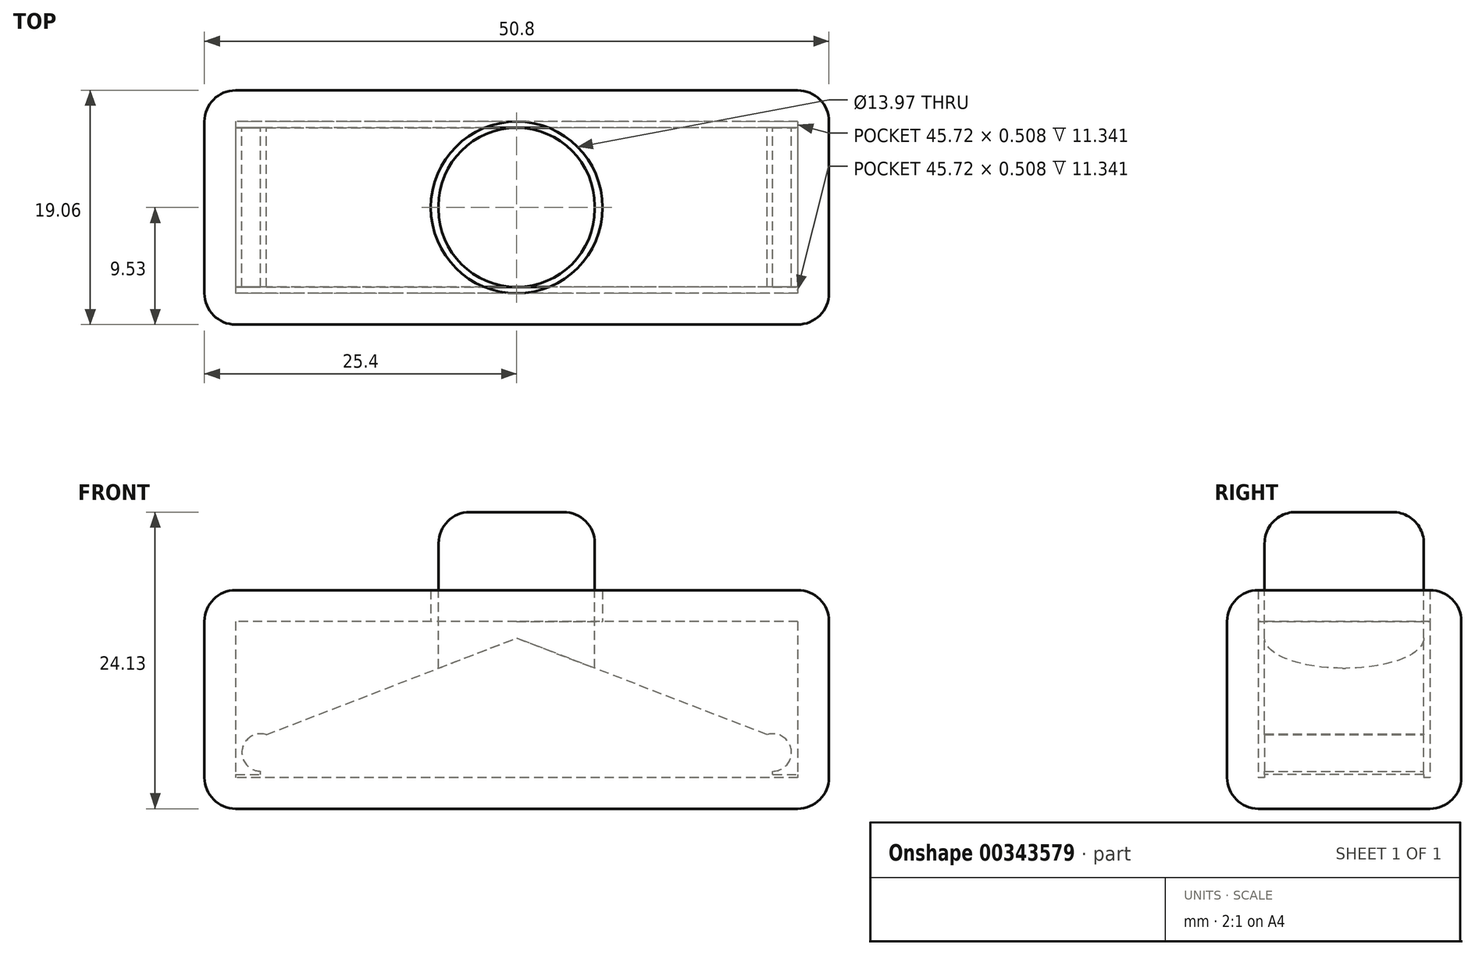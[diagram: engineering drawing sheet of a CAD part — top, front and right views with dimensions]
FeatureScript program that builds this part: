
annotation { "Feature Type Name" : "Feature", "Feature Type Description" : "" }
export const myFeature = defineFeature(function(context is Context, id is Id, definition is map)
    precondition{}
    {
        {
            var Q0;
            Q0=qCreatedBy(makeId("Top.planeOp"),FACE);
            var sketch = newSketch(context, id + "F0", { "sketchPlane" : qUnion([Q0])});
            skLineSegment(sketch, "E0.bottom", {"start": v(25.4, 9.53) * mm, "end": v(-25.4, 9.53) * mm});
            skLineSegment(sketch, "E0.top", {"start": v(25.4, -9.53) * mm, "end": v(-25.4, -9.53) * mm});
            skLineSegment(sketch, "E0.left", {"start": v(25.4, 9.53) * mm, "end": v(25.4, -9.53) * mm});
            skLineSegment(sketch, "E0.right", {"start": v(-25.4, 9.53) * mm, "end": v(-25.4, -9.53) * mm});
            skPoint(sketch, "E0.middle", {"position": v(0, 0) * mm});
            skLineSegment(sketch, "E1.bottom", {"start": v(22.86, 6.99) * mm, "end": v(-22.86, 6.99) * mm});
            skLineSegment(sketch, "E1.top", {"start": v(22.86, -6.99) * mm, "end": v(-22.86, -6.99) * mm});
            skLineSegment(sketch, "E1.left", {"start": v(22.86, 6.98) * mm, "end": v(22.86, -6.99) * mm});
            skLineSegment(sketch, "E1.right", {"start": v(-22.86, 6.99) * mm, "end": v(-22.86, -6.98) * mm});
            skSolve(sketch);
        }
        {
            var Q0;
            Q0 = qSketchRegion(id + "F0", true);
            extrude(context, id + "F1", {"entities" : qUnion([Q0]), "depth" : 12.7 * mm, "offsetDistance" : 25.4 * mm});
        }
        {
            var Q0;
            Q0=makeQuery(id+"F1.opExtrude","CAP_FACE",FACE,{"disambiguationData":[OSD([sQuery(id+"F0.wireOp",EDGE,"E0.bottom"),sQuery(id+"F0.wireOp",EDGE,"E0.top"),sQuery(id+"F0.wireOp",EDGE,"E0.left"),sQuery(id+"F0.wireOp",EDGE,"E0.right"),sQuery(id+"F0.wireOp",EDGE,"E1.bottom"),sQuery(id+"F0.wireOp",EDGE,"E1.top"),sQuery(id+"F0.wireOp",EDGE,"E1.left"),sQuery(id+"F0.wireOp",EDGE,"E1.right")])],"isStart":true});
            var sketch = newSketch(context, id + "F2", { "sketchPlane" : qUnion([Q0])});
            skLineSegment(sketch, "E2.bottom", {"start": v(25.4, 9.53) * mm, "end": v(-25.4, 9.53) * mm});
            skLineSegment(sketch, "E2.top", {"start": v(25.4, -9.53) * mm, "end": v(-25.4, -9.53) * mm});
            skLineSegment(sketch, "E2.left", {"start": v(25.4, 9.53) * mm, "end": v(25.4, -9.53) * mm});
            skLineSegment(sketch, "E2.right", {"start": v(-25.4, 9.53) * mm, "end": v(-25.4, -9.53) * mm});
            skSolve(sketch);
        }
        {
            var Q0;
            Q0 = qSketchRegion(id + "F2", true);
            extrude(context, id + "F3", {"entities" : qUnion([Q0]), "operationType" : NewBodyOperationType.ADD, "depth" : 2.54 * mm, "offsetDistance" : 25.4 * mm});
        }
        {
            var Q0;
            Q0=makeQuery(id+"F1.opExtrude","SWEPT_FACE",FACE,{"disambiguationData":[OSD([sQuery(id+"F0.wireOp",EDGE,"E1.bottom")])]});
            var sketch = newSketch(context, id + "F4", { "sketchPlane" : qUnion([Q0])});
            skLineSegment(sketch, "E3.bottom", {"start": v(-25.4, -2.54) * mm, "end": v(25.4, -2.54) * mm});
            skLineSegment(sketch, "E3.top", {"start": v(-25.4, -2.54) * mm, "end": v(25.4, -2.54) * mm});
            skLineSegment(sketch, "E3.left", {"start": v(-25.4, -2.54) * mm, "end": v(-25.4, -2.54) * mm});
            skLineSegment(sketch, "E3.right", {"start": v(25.4, -2.54) * mm, "end": v(25.4, -2.54) * mm});
            skLineSegment(sketch, "E4.top", {"start": v(-25.4, 0.25) * mm, "end": v(25.4, 0.25) * mm});
            skLineSegment(sketch, "E4.left", {"start": v(-25.4, -2.54) * mm, "end": v(-25.4, 0.25) * mm});
            skLineSegment(sketch, "E4.right", {"start": v(25.4, -2.54) * mm, "end": v(25.4, 0.25) * mm});
            skLineSegment(sketch, "E5", {"start": v(25.4, 12.7) * mm, "end": v(-25.4, 12.7) * mm});
            skLineSegment(sketch, "E6.bottom", {"start": v(6.35, 7.62) * mm, "end": v(-6.35, 7.62) * mm});
            skLineSegment(sketch, "E6.top", {"start": v(6.35, 17.78) * mm, "end": v(-6.35, 17.78) * mm});
            skLineSegment(sketch, "E6.left", {"start": v(6.35, 7.62) * mm, "end": v(6.35, 17.78) * mm});
            skLineSegment(sketch, "E6.right", {"start": v(-6.35, 7.62) * mm, "end": v(-6.35, 17.78) * mm});
            skPoint(sketch, "E6.middle", {"position": v(0, 12.7) * mm});
            skLineSegment(sketch, "E7", {"start": v(6.35, 7.62) * mm, "end": v(5.08, 7.62) * mm});
            skLineSegment(sketch, "E8", {"start": v(6.35, 7.62) * mm, "end": v(6.35, 8.89) * mm});
            skLineSegment(sketch, "E9", {"start": v(-6.35, 7.62) * mm, "end": v(-5.08, 7.62) * mm});
            skLineSegment(sketch, "E10", {"start": v(-6.35, 7.62) * mm, "end": v(-6.35, 8.89) * mm});
            skLineSegment(sketch, "E11", {"start": v(-25.4, 0.25) * mm, "end": v(-20.83, 0.25) * mm});
            skLineSegment(sketch, "E12", {"start": v(-20.83, 0.25) * mm, "end": v(-20.83, 2.03) * mm});
            skCircle(sketch, "E13", {"center": v(-20.83, 2.03) * mm, "radius": 1.52 * mm});
            skLineSegment(sketch, "E14", {"start": v(-20.83, 2.03) * mm, "end": v(-19.56, 2.03) * mm});
            skLineSegment(sketch, "E15", {"start": v(-20.83, 2.03) * mm, "end": v(-20.83, 3.3) * mm});
            skLineSegment(sketch, "E16", {"start": v(-20.83, 3.3) * mm, "end": v(-6.35, 8.89) * mm});
            skLineSegment(sketch, "E17", {"start": v(25.4, -2.54) * mm, "end": v(20.83, -2.54) * mm});
            skLineSegment(sketch, "E18", {"start": v(20.83, -2.54) * mm, "end": v(20.83, 2.03) * mm});
            skCircle(sketch, "E19", {"center": v(20.83, 2.03) * mm, "radius": 1.52 * mm});
            skLineSegment(sketch, "E20", {"start": v(20.83, 2.03) * mm, "end": v(20.83, 3.3) * mm});
            skLineSegment(sketch, "E21", {"start": v(20.83, 2.03) * mm, "end": v(19.56, 2.03) * mm});
            skLineSegment(sketch, "E22", {"start": v(20.83, 3.3) * mm, "end": v(6.35, 8.89) * mm});
            skLineSegment(sketch, "E23", {"start": v(19.56, 2.03) * mm, "end": v(5.08, 7.62) * mm});
            skLineSegment(sketch, "E24", {"start": v(-19.56, 2.03) * mm, "end": v(-5.08, 7.62) * mm});
            skLineSegment(sketch, "E25.bottom", {"start": v(-6.35, 17.78) * mm, "end": v(6.35, 17.78) * mm});
            skLineSegment(sketch, "E25.top", {"start": v(-6.35, 21.59) * mm, "end": v(6.35, 21.59) * mm});
            skLineSegment(sketch, "E25.left", {"start": v(-6.35, 17.78) * mm, "end": v(-6.35, 21.59) * mm});
            skLineSegment(sketch, "E25.right", {"start": v(6.35, 17.78) * mm, "end": v(6.35, 21.59) * mm});
            skSolve(sketch);
        }
        {
            var Q0;
            Q0 = qSketchRegion(id + "F4", true);
            extrude(context, id + "F5", {"entities" : qUnion([Q0]), "operationType" : NewBodyOperationType.ADD, "depth" : 13.46 * mm, "offsetDistance" : 25.4 * mm, "hasSecondDirection" : true, "secondDirectionOppositeDirection" : true, "secondDirectionDepth" : -0.5 * mm});
        }
        {
            var Q0;
            Q0=makeQuery(id+"F5.opExtrude","CAP_EDGE",EDGE,{"disambiguationData":[OSD([sQuery(id+"F4.wireOp",EDGE,"E6.right")])],"isStart":false});
            var Q1;
            Q1=makeQuery(id+"F5.opExtrude","CAP_EDGE",EDGE,{"disambiguationData":[OSD([sQuery(id+"F4.wireOp",EDGE,"E6.left")])],"isStart":false});
            var Q2;
            Q2=makeQuery(id+"F5.opExtrude","CAP_EDGE",EDGE,{"disambiguationData":[OSD([sQuery(id+"F4.wireOp",EDGE,"E6.left")])],"isStart":true});
            var Q3;
            Q3=makeQuery(id+"F5.opExtrude","CAP_EDGE",EDGE,{"disambiguationData":[OSD([sQuery(id+"F4.wireOp",EDGE,"E6.right")])],"isStart":true});
            fillet(context, id + "F6", {"entities" : qUnion([Q0, Q1, Q2, Q3]), "tangentPropagation" : true, "radius" : 6.35 * mm, "defaultsChanged" : true, "vertexSettings" : [], "allowEdgeOverflow" : false});
        }
        {
            var Q0;
            Q0=makeQuery(id+"F1.opExtrude","CAP_FACE",FACE,{"disambiguationData":[OSD([sQuery(id+"F0.wireOp",EDGE,"E0.bottom"),sQuery(id+"F0.wireOp",EDGE,"E0.top"),sQuery(id+"F0.wireOp",EDGE,"E0.left"),sQuery(id+"F0.wireOp",EDGE,"E0.right"),sQuery(id+"F0.wireOp",EDGE,"E1.bottom"),sQuery(id+"F0.wireOp",EDGE,"E1.top"),sQuery(id+"F0.wireOp",EDGE,"E1.left"),sQuery(id+"F0.wireOp",EDGE,"E1.right")])],"isStart":false});
            var sketch = newSketch(context, id + "F7", { "sketchPlane" : qUnion([Q0])});
            skLineSegment(sketch, "E26.bottom", {"start": v(-25.4, 9.53) * mm, "end": v(25.4, 9.53) * mm});
            skLineSegment(sketch, "E26.top", {"start": v(-25.4, -9.53) * mm, "end": v(25.4, -9.53) * mm});
            skLineSegment(sketch, "E26.left", {"start": v(-25.4, 9.53) * mm, "end": v(-25.4, -9.53) * mm});
            skLineSegment(sketch, "E26.right", {"start": v(25.4, 9.53) * mm, "end": v(25.4, -9.53) * mm});
            skCircle(sketch, "E27", {"center": v(0, 0) * mm, "radius": 6.99 * mm});
            skSolve(sketch);
        }
        {
            var Q0;
            Q0 = qSketchRegion(id + "F7", true);
            extrude(context, id + "F8", {"entities" : qUnion([Q0]), "operationType" : NewBodyOperationType.ADD, "depth" : 2.54 * mm, "offsetDistance" : 25.4 * mm});
        }
        {
            var Q0;
            Q0=makeQuery(id+"F8.boolean.opBoolean","MERGE",EDGE,{"derivedFrom":[makeQuery(id+"F3.boolean.opBoolean","MERGE",EDGE,{"derivedFrom":[makeQuery(id+"F1.opExtrude","SWEPT_EDGE",EDGE,{"disambiguationData":[OSD([sQuery(id+"F0.wireOp",EDGE,"E0.bottom"),sQuery(id+"F0.wireOp",EDGE,"E0.right")])]}),makeQuery(id+"F3.opExtrude","SWEPT_EDGE",EDGE,{"disambiguationData":[OSD([sQuery(id+"F2.wireOp",EDGE,"E2.top"),sQuery(id+"F2.wireOp",EDGE,"E2.right")])]})]}),makeQuery(id+"F8.opExtrude","SWEPT_EDGE",EDGE,{"disambiguationData":[OSD([sQuery(id+"F7.wireOp",EDGE,"E26.bottom"),sQuery(id+"F7.wireOp",EDGE,"E26.left")])]})]});
            var Q1;
            Q1=makeQuery(id+"F8.opExtrude","CAP_EDGE",EDGE,{"disambiguationData":[OSD([sQuery(id+"F7.wireOp",EDGE,"E26.left")])],"isStart":false});
            var Q2;
            Q2=makeQuery(id+"F8.boolean.opBoolean","MERGE",EDGE,{"derivedFrom":[makeQuery(id+"F3.boolean.opBoolean","MERGE",EDGE,{"derivedFrom":[makeQuery(id+"F1.opExtrude","SWEPT_EDGE",EDGE,{"disambiguationData":[OSD([sQuery(id+"F0.wireOp",EDGE,"E0.top"),sQuery(id+"F0.wireOp",EDGE,"E0.right")])]}),makeQuery(id+"F3.opExtrude","SWEPT_EDGE",EDGE,{"disambiguationData":[OSD([sQuery(id+"F2.wireOp",EDGE,"E2.bottom"),sQuery(id+"F2.wireOp",EDGE,"E2.right")])]})]}),makeQuery(id+"F8.opExtrude","SWEPT_EDGE",EDGE,{"disambiguationData":[OSD([sQuery(id+"F7.wireOp",EDGE,"E26.top"),sQuery(id+"F7.wireOp",EDGE,"E26.left")])]})]});
            var Q3;
            Q3=makeQuery(id+"F3.opExtrude","CAP_EDGE",EDGE,{"disambiguationData":[OSD([sQuery(id+"F2.wireOp",EDGE,"E2.right")])],"isStart":false});
            var Q4;
            Q4=makeQuery(id+"F8.boolean.opBoolean","MERGE",EDGE,{"derivedFrom":[makeQuery(id+"F3.boolean.opBoolean","MERGE",EDGE,{"derivedFrom":[makeQuery(id+"F1.opExtrude","SWEPT_EDGE",EDGE,{"disambiguationData":[OSD([sQuery(id+"F0.wireOp",EDGE,"E0.bottom"),sQuery(id+"F0.wireOp",EDGE,"E0.left")])]}),makeQuery(id+"F3.opExtrude","SWEPT_EDGE",EDGE,{"disambiguationData":[OSD([sQuery(id+"F2.wireOp",EDGE,"E2.top"),sQuery(id+"F2.wireOp",EDGE,"E2.left")])]})]}),makeQuery(id+"F8.opExtrude","SWEPT_EDGE",EDGE,{"disambiguationData":[OSD([sQuery(id+"F7.wireOp",EDGE,"E26.bottom"),sQuery(id+"F7.wireOp",EDGE,"E26.right")])]})]});
            var Q5;
            Q5=makeQuery(id+"F3.opExtrude","CAP_EDGE",EDGE,{"disambiguationData":[OSD([sQuery(id+"F2.wireOp",EDGE,"E2.left")])],"isStart":false});
            var Q6;
            Q6=makeQuery(id+"F8.boolean.opBoolean","MERGE",EDGE,{"derivedFrom":[makeQuery(id+"F3.boolean.opBoolean","MERGE",EDGE,{"derivedFrom":[makeQuery(id+"F1.opExtrude","SWEPT_EDGE",EDGE,{"disambiguationData":[OSD([sQuery(id+"F0.wireOp",EDGE,"E0.top"),sQuery(id+"F0.wireOp",EDGE,"E0.left")])]}),makeQuery(id+"F3.opExtrude","SWEPT_EDGE",EDGE,{"disambiguationData":[OSD([sQuery(id+"F2.wireOp",EDGE,"E2.bottom"),sQuery(id+"F2.wireOp",EDGE,"E2.left")])]})]}),makeQuery(id+"F8.opExtrude","SWEPT_EDGE",EDGE,{"disambiguationData":[OSD([sQuery(id+"F7.wireOp",EDGE,"E26.top"),sQuery(id+"F7.wireOp",EDGE,"E26.right")])]})]});
            var Q7;
            Q7=makeQuery(id+"F8.opExtrude","CAP_EDGE",EDGE,{"disambiguationData":[OSD([sQuery(id+"F7.wireOp",EDGE,"E26.right")])],"isStart":false});
            var Q8;
            Q8=makeQuery(id+"F8.opExtrude","CAP_EDGE",EDGE,{"disambiguationData":[OSD([sQuery(id+"F7.wireOp",EDGE,"E26.top")])],"isStart":false});
            var Q9;
            Q9=makeQuery(id+"F3.opExtrude","CAP_EDGE",EDGE,{"disambiguationData":[OSD([sQuery(id+"F2.wireOp",EDGE,"E2.bottom")])],"isStart":false});
            var Q10;
            Q10=makeQuery(id+"F3.opExtrude","CAP_EDGE",EDGE,{"disambiguationData":[OSD([sQuery(id+"F2.wireOp",EDGE,"E2.top")])],"isStart":false});
            var Q11;
            Q11=makeQuery(id+"F8.opExtrude","CAP_EDGE",EDGE,{"disambiguationData":[OSD([sQuery(id+"F7.wireOp",EDGE,"E26.bottom")])],"isStart":false});
            fillet(context, id + "F9", {"entities" : qUnion([Q0, Q1, Q2, Q3, Q4, Q5, Q6, Q7, Q8, Q9, Q10, Q11]), "tangentPropagation" : true, "radius" : 2.54 * mm, "defaultsChanged" : false, "vertexSettings" : [], "allowEdgeOverflow" : false});
        }
        {
            var Q0;
            Q0=makeQuery(id+"F6.opFillet","BLEND_EDGE",EDGE,{"blendedFrom":[makeQuery(id+"F5.opExtrude","CAP_EDGE",EDGE,{"disambiguationData":[OSD([sQuery(id+"F4.wireOp",EDGE,"E6.left"),sQuery(id+"F4.wireOp",EDGE,"E25.right")])],"isStart":false}),makeQuery(id+"F5.opExtrude","SWEPT_FACE",FACE,{"disambiguationData":[OSD([sQuery(id+"F4.wireOp",EDGE,"E25.top")])]})],"blendedInto":[makeQuery(id+"F5.opExtrude","SWEPT_FACE",FACE,{"disambiguationData":[OSD([sQuery(id+"F4.wireOp",EDGE,"E25.top")])]})]});
            fillet(context, id + "F10", {"entities" : qUnion([Q0]), "tangentPropagation" : true, "radius" : 2.54 * mm, "defaultsChanged" : true, "vertexSettings" : [], "allowEdgeOverflow" : false});
        }
    });
